FCSTD DOCUMENT  (FreeCAD 1.0R39109 (Git))
Label: main_bass
License: All rights reserved
LicenseURL: https://en.wikipedia.org/wiki/All_rights_reserved
objects: Sketcher::SketchObject×1, PartDesign::Body×1
note: 3 computed .brp shape members not serialized (recipe doc carries the construction recipe); baked Part::Feature solids carry a one-line shape summary decoded from their .brp

FEATURE [Sketcher::SketchObject] Sketch
  ArcFitTolerance = 1e-06
  AttachmentSupport = -> [XY_Plane]
  FullyConstrained = true
  MakeInternals = false
  MapMode = 5
  sketch-geometry (48):
    g0: LineSegment StartX=-100 StartY=100 StartZ=0 EndX=-100 EndY=-100 EndZ=0
    g1: LineSegment StartX=100 StartY=-50 StartZ=0 EndX=100 EndY=100 EndZ=0
    g2: LineSegment StartX=100 StartY=100 StartZ=0 EndX=-100 EndY=100 EndZ=0
    g3: Circle CenterX=-82.5 CenterY=82.5 CenterZ=0 NormalX=0 NormalY=0 NormalZ=1 AngleXU=0 Radius=7.75
    g4: Circle CenterX=82.5 CenterY=82.5 CenterZ=0 NormalX=0 NormalY=0 NormalZ=1 AngleXU=0 Radius=7.75
    g5: Circle CenterX=-82.5 CenterY=-82.5 CenterZ=0 NormalX=0 NormalY=0 NormalZ=1 AngleXU=0 Radius=7.75
    g6: LineSegment [constr] StartX=-95 StartY=95 StartZ=0 EndX=-95 EndY=70 EndZ=0
    g7: LineSegment [constr] StartX=-95 StartY=70 StartZ=0 EndX=-70 EndY=70 EndZ=0
    g8: LineSegment [constr] StartX=-70 StartY=70 StartZ=0 EndX=-70 EndY=95 EndZ=0
    g9: LineSegment [constr] StartX=-70 StartY=95 StartZ=0 EndX=-95 EndY=95 EndZ=0
    g10: Circle CenterX=-95 CenterY=95 CenterZ=0 NormalX=0 NormalY=0 NormalZ=1 AngleXU=0 Radius=1.5
    g11: Circle CenterX=-70 CenterY=95 CenterZ=0 NormalX=0 NormalY=0 NormalZ=1 AngleXU=0 Radius=1.5
    g12: Circle CenterX=-70 CenterY=70 CenterZ=0 NormalX=0 NormalY=0 NormalZ=1 AngleXU=0 Radius=1.5
    g13: Circle CenterX=-95 CenterY=70 CenterZ=0 NormalX=0 NormalY=0 NormalZ=1 AngleXU=0 Radius=1.5
    g14: LineSegment [constr] StartX=70 StartY=95 StartZ=0 EndX=70 EndY=70 EndZ=0
    g15: LineSegment [constr] StartX=70 StartY=70 StartZ=0 EndX=95 EndY=70 EndZ=0
    g16: LineSegment [constr] StartX=95 StartY=70 StartZ=0 EndX=95 EndY=95 EndZ=0
    g17: LineSegment [constr] StartX=95 StartY=95 StartZ=0 EndX=70 EndY=95 EndZ=0
    g18: Circle CenterX=70 CenterY=95 CenterZ=0 NormalX=0 NormalY=0 NormalZ=1 AngleXU=0 Radius=1.5
    g19: Circle CenterX=95 CenterY=95 CenterZ=0 NormalX=0 NormalY=0 NormalZ=1 AngleXU=0 Radius=1.5
    g20: Circle CenterX=95 CenterY=70 CenterZ=0 NormalX=0 NormalY=0 NormalZ=1 AngleXU=0 Radius=1.5
    g21: Circle CenterX=70 CenterY=70 CenterZ=0 NormalX=0 NormalY=0 NormalZ=1 AngleXU=0 Radius=1.5
    g22: LineSegment [constr] StartX=-95 StartY=-70 StartZ=0 EndX=-95 EndY=-95 EndZ=0
    g23: LineSegment [constr] StartX=-95 StartY=-95 StartZ=0 EndX=-70 EndY=-95 EndZ=0
    g24: LineSegment [constr] StartX=-70 StartY=-95 StartZ=0 EndX=-70 EndY=-70 EndZ=0
    g25: LineSegment [constr] StartX=-70 StartY=-70 StartZ=0 EndX=-95 EndY=-70 EndZ=0
    g26: Circle CenterX=-95 CenterY=-70 CenterZ=0 NormalX=0 NormalY=0 NormalZ=1 AngleXU=0 Radius=1.5
    g27: Circle CenterX=-70 CenterY=-70 CenterZ=0 NormalX=0 NormalY=0 NormalZ=1 AngleXU=0 Radius=1.5
    g28: Circle CenterX=-70 CenterY=-95 CenterZ=0 NormalX=0 NormalY=0 NormalZ=1 AngleXU=0 Radius=1.5
    g29: Circle CenterX=-95 CenterY=-95 CenterZ=0 NormalX=0 NormalY=0 NormalZ=1 AngleXU=0 Radius=1.5
    g30: Circle CenterX=0 CenterY=0 CenterZ=0 NormalX=0 NormalY=0 NormalZ=1 AngleXU=0 Radius=62.5
    g31: Circle CenterX=0 CenterY=74.25 CenterZ=0 NormalX=0 NormalY=0 NormalZ=1 AngleXU=0 Radius=4
    g32: Circle CenterX=-85.5 CenterY=0 CenterZ=0 NormalX=0 NormalY=0 NormalZ=1 AngleXU=0 Radius=5.25
    g33: Circle [constr] CenterX=-85.5 CenterY=0 CenterZ=0 NormalX=0 NormalY=0 NormalZ=1 AngleXU=0 Radius=11.25
    g34: Circle [constr] CenterX=-85.5 CenterY=0 CenterZ=0 NormalX=0 NormalY=0 NormalZ=1 AngleXU=0 Radius=8
    g35: Circle CenterX=-85.5 CenterY=8 CenterZ=0 NormalX=0 NormalY=0 NormalZ=1 AngleXU=0 Radius=1.5
    g36: Circle CenterX=-77.5 CenterY=0 CenterZ=0 NormalX=0 NormalY=0 NormalZ=1 AngleXU=0 Radius=1.5
    g37: Circle CenterX=-85.5 CenterY=-8 CenterZ=0 NormalX=0 NormalY=0 NormalZ=1 AngleXU=0 Radius=1.5
    g38: Circle CenterX=-93.5 CenterY=0 CenterZ=0 NormalX=0 NormalY=0 NormalZ=1 AngleXU=0 Radius=1.5
    g39: LineSegment StartX=20 StartY=-100 StartZ=0 EndX=20 EndY=-67 EndZ=0
    g40: LineSegment StartX=20 StartY=-67 StartZ=0 EndX=48 EndY=-67 EndZ=0
    g41: LineSegment StartX=48 StartY=-67 StartZ=0 EndX=48 EndY=-58 EndZ=0
    g42: LineSegment StartX=48 StartY=-58 StartZ=0 EndX=55 EndY=-58 EndZ=0
    g43: LineSegment StartX=55 StartY=-58 StartZ=0 EndX=55 EndY=-50 EndZ=0
    g44: LineSegment StartX=55 StartY=-50 StartZ=0 EndX=100 EndY=-50 EndZ=0
    g45: LineSegment StartX=-100 StartY=-100 StartZ=0 EndX=20 EndY=-100 EndZ=0
    g46: Circle CenterX=62.5 CenterY=-45 CenterZ=0 NormalX=0 NormalY=0 NormalZ=1 AngleXU=0 Radius=1.5
    g47: Circle CenterX=92.5 CenterY=-45 CenterZ=0 NormalX=0 NormalY=0 NormalZ=1 AngleXU=0 Radius=1.5
  constraints (126):
    c: Coincident(g1,g2)
    c: Coincident(g2,g0)
    c: Vertical(g0)
    c: Vertical(g1)
    c: Horizontal(g2)
    c: DistanceX(g-1,g1) = 100
    c: DistanceY(g-1,g1) = 100
    c: Horizontal(g3,g4)
    c: Vertical(g3,g5)
    c: DistanceY(g-1,g4) = 82.5
    c: DistanceX(g-1,g4) = 82.5
    c: DistanceX(g3,g-1) = 82.5
    c: DistanceY(g5,g-1) = 82.5
    c: Diameter(g5) = 15.5
    c: Equal(g3,g5)
    c: Equal(g5,g4)
    c: Coincident(g6,g7)
    c: Coincident(g7,g8)
    c: Coincident(g8,g9)
    c: Coincident(g9,g6)
    c: Vertical(g6)
    c: Vertical(g8)
    c: Horizontal(g7)
    c: Horizontal(g9)
    c: Equal(g9,g8)
    c: DistanceX(g9,g9) = 25
    c: Symmetric(g6,g7,g3)
    c: Coincident(g10,g6)
    c: Coincident(g11,g8)
    c: Coincident(g12,g7)
    c: Coincident(g13,g6)
    c: Equal(g10,g11)
    c: Equal(g11,g12)
    c: Equal(g12,g13)
    c: Diameter(g11) = 3
    c: Coincident(g14,g15)
    c: Coincident(g15,g16)
    c: Coincident(g16,g17)
    c: Coincident(g17,g14)
    c: Vertical(g14)
    c: Vertical(g16)
    c: Horizontal(g15)
    c: Horizontal(g17)
    c: Equal(g17,g14)
    c: Equal(g14,g8)
    c: Symmetric(g14,g15,g4)
    c: Coincident(g18,g14)
    c: Coincident(g19,g16)
    c: Coincident(g20,g15)
    c: Coincident(g21,g14)
    c: Equal(g18,g19)
    c: Equal(g19,g20)
    c: Equal(g20,g21)
    c: Equal(g12,g21)
    c: Coincident(g22,g23)
    c: Coincident(g23,g24)
    c: Coincident(g24,g25)
    c: Coincident(g25,g22)
    c: Vertical(g22)
    c: Vertical(g24)
    c: Horizontal(g23)
    c: Horizontal(g25)
    c: Equal(g25,g24)
    c: Equal(g25,g7)
    c: Symmetric(g22,g23,g5)
    c: Coincident(g26,g22)
    c: Coincident(g27,g24)
    c: Coincident(g28,g23)
    c: Coincident(g29,g22)
    c: Equal(g26,g27)
    c: Equal(g27,g28)
    c: Equal(g28,g29)
    c: Equal(g26,g13)
    c: Coincident(g30,g-1)
    c: Diameter(g30) = 125
    c: PointOnObject(g31,g-2)
    c: Diameter(g31) = 8
    c: DistanceY(g-1,g31) = 74.25
    c: PointOnObject(g32,g-1)
    c: Coincident(g33,g32)
    c: Diameter(g32) = 10.5
    c: Diameter(g33) = 22.5
    c: DistanceX(g32,g-1) = 85.5
    c: Coincident(g34,g32)
    c: Diameter(g34) = 16
    c: PointOnObject(g35,g34)
    c: PointOnObject(g36,g34)
    c: PointOnObject(g37,g34)
    c: PointOnObject(g38,g34)
    c: Vertical(g35,g37)
    c: Vertical(g37,g32)
    c: Horizontal(g32,g36)
    c: Horizontal(g32,g38)
    c: Equal(g36,g35)
    c: Equal(g38,g37)
    c: Equal(g37,g36)
    c: Diameter(g36) = 3
    c: Vertical(g39)
    c: Coincident(g39,g40)
    c: Horizontal(g40)
    c: Coincident(g40,g41)
    c: Coincident(g41,g42)
    c: Horizontal(g42)
    c: Coincident(g42,g43)
    c: Coincident(g43,g44)
    c: Horizontal(g44)
    c: DistanceY(g39,g39) = 33
    c: DistanceX(g40,g40) = 28
    c: DistanceX(g42,g42) = 7
    c: Vertical(g43)
    c: Vertical(g41)
    c: DistanceY(g43,g43) = 8
    c: DistanceX(g44,g44) = 45
    c: DistanceY(g41,g41) = 9
    c: Coincident(g1,g44)
    c: Coincident(g45,g0)
    c: Coincident(g45,g39)
    c: Horizontal(g45)
    c: DistanceX(g2,g2) = 200
    c: DistanceY(g0,g0) = 200
    c: DistanceX(g46,g47) = 30
    c: DistanceX(g47,g1) = 7.5
    c: DistanceY(g1,g47) = 5
    c: Equal(g46,g47)
    c: Diameter(g47) = 3
    c: Horizontal(g46,g47)
FEATURE [PartDesign::Body] Body
  AllowCompound = false
  Group = -> [Sketch]
  Origin = -> Origin
